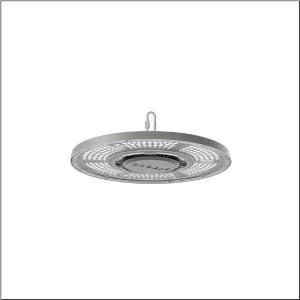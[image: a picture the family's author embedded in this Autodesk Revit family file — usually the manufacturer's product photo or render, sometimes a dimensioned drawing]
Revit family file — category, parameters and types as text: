
# Revit family: highbay_31-s_51hc41da4fmb
name_source: partatom
category: Lighting Fixtures
units: mm (PartAtom-declared; Revit-internal decimal feet)

## family parameters
Cut with Voids When Loaded = No
Host = Face
Light Source = No
Part Type = Normal
Room Calculation Point = No
Round Connector Dimension = Use Diameter
Shared = No

## types (1)
- Highbay 31-S (1 x LED, 14000 lm, 94 W, 4000K)
    Apparent Load = 94 VA
    CIE Flux Codes = 94 98 100 100 100
    Color Rendering = 80
    Color Temperature = 4000K
    Default Elevation = 1800 mm
    Description = Highbay 31-S, LED high bay luminaire, primary light control with lens, of PC, primary optical cover: cover panel, of PC, transparent, light emission: direct distribution, primary light characteristic: rotationally symmetric, installation type: suspended mounting, surface-mounted, LED, rated luminous flux: 14.000lm, luminous efficacy: 150lm/W, light colour: 840, colour temperature: 4000K, control gear: ECG DALI, with cable, 5x 1.0mm², free wire ends, mains connection: 220..240V, AC/DC, 0/50..60Hz, cable length: 1,5m, rated input power: 94W, housing, rotationally symmetric, of diecast aluminium, powder-coated, grey aluminium (RAL 9007), with hook on luminaire side, incl. screw, diameter: 339mm, protection rating (complete): IP65, insulation class (complete): insulation class I (protective earthing), certification: CE, ENEC, UKCA, protection symbol: D, impact resistance: IK08, permissible operating ambient temperature: -30..+45°C, standard: EN 60598-2-22, EN 60598, corresponds to IFS (International Featured Standards) requirements for safety and quality in the food industry, packaging unit: 1 piece
    Height = 141 mm
    Lamp = 1 x LED
    Lamp Light Flux = 14000 lm
    Lamp Power = 94 W
    Lamp count = 1
    Length = 339 mm
    Luminous efficacy = 149 lm/W
    Manufacturer = Siteco
    ModVariant = No
    Model = 51HC41DA4FMB
    Mounting Place = Ceiling
    Mounting Type = Pendant
    Number of Poles = 1
    OnlyDefault = Yes
    Power Factor = 1
    Product Name = Highbay 31-S
    Product group = LED high bay luminaire
    ProductGroupID = 903
    Protection Class = Protection class I
    Protection Degree = IP 65
    RLX_Detail_Level = 1
    RLX_Emergency_Light_Flux = 0 lm
    RLX_Emergency_Type = 0
    RLX_Emergency_Type_DB = No
    RlxData = <blob elided: 107169 chars, md5=1a37a15c>
    Socket = socket
    Standby Power = 0 W
    System Light Flux = 14000 lm
    System Power = 94 W
    Type Comments = Product without accessories
    Type Image = l_1007237.jpg
    URL = http://relux.com
    VarID = ---
    Voltage = 0 V
    Weight = 0.00 kg
    Width = 0 mm  [stored 0 ft]

note: [stored X ft] marks values corroborated as IEEE doubles in the binary element streams (Revit-internal decimal feet)

## geometry (parser evidence)
native form markers: Blend x4, Sweep x10
no freeform markers — native parametric forms only
